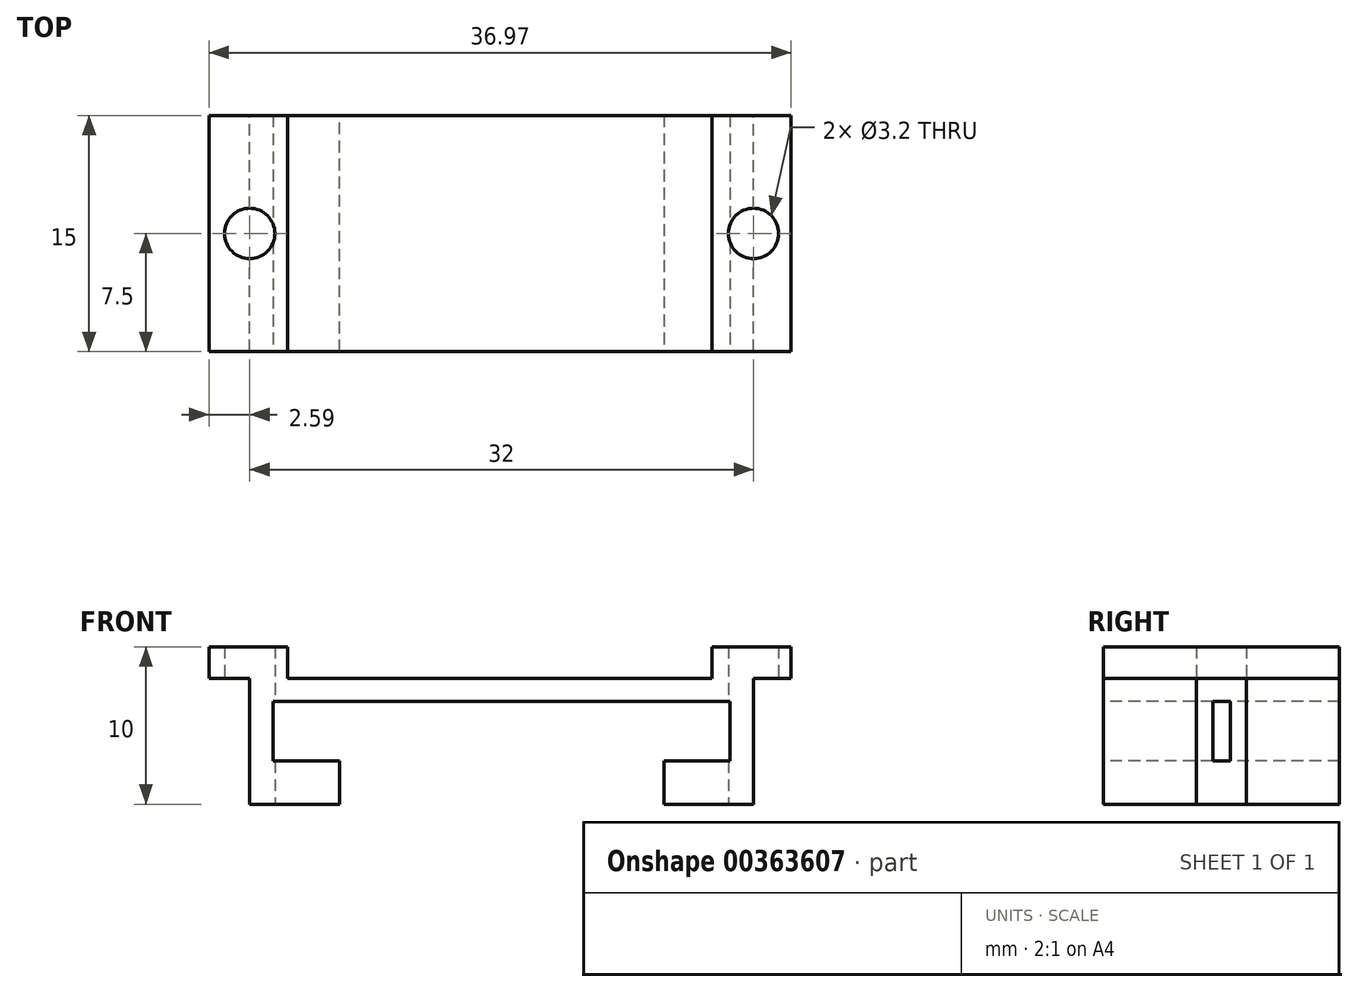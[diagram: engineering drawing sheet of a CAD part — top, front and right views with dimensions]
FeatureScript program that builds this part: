
annotation { "Feature Type Name" : "Feature", "Feature Type Description" : "" }
export const myFeature = defineFeature(function(context is Context, id is Id, definition is map)
    precondition{}
    {
        {
            var Q0;
            Q0=qCreatedBy(makeId("Top.planeOp"),FACE);
            var sketch = newSketch(context, id + "F0", { "sketchPlane" : qUnion([Q0])});
            skLineSegment(sketch, "E0.bottom", {"start": v(16, -7.5) * mm, "end": v(-16, -7.5) * mm});
            skLineSegment(sketch, "E0.top", {"start": v(16, 7.5) * mm, "end": v(-16, 7.5) * mm});
            skLineSegment(sketch, "E0.left", {"start": v(16, -7.5) * mm, "end": v(16, 7.5) * mm});
            skLineSegment(sketch, "E0.right", {"start": v(-16, -7.5) * mm, "end": v(-16, 7.5) * mm});
            skPoint(sketch, "E0.middle", {"position": v(0, 0) * mm});
            skSolve(sketch);
        }
        {
            var Q0;
            Q0=makeQuery(id+"F0.imprint","IMPRINT",FACE,{"disambiguationData":[TD([[makeQuery(id+"F0.imprint","IMPRINT",EDGE,{"derivedFrom":sQuery(id+"F0.wireOp",EDGE,"E0.bottom")}),-1.0]])]});
            extrude(context, id + "F1", {"entities" : qUnion([Q0]), "depth" : 8 * mm});
        }
        {
            var Q0;
            Q0=makeQuery(id+"F1.opExtrude","SWEPT_FACE",FACE,{"disambiguationData":[OSD([sQuery(id+"F0.wireOp",EDGE,"E0.bottom")])]});
            var sketch = newSketch(context, id + "F2", { "sketchPlane" : qUnion([Q0])});
            skLineSegment(sketch, "E1.bottom", {"start": v(14.5, 2.74) * mm, "end": v(-14.5, 2.74) * mm});
            skLineSegment(sketch, "E1.top", {"start": v(14.5, 6.54) * mm, "end": v(-14.5, 6.54) * mm});
            skLineSegment(sketch, "E1.left", {"start": v(14.5, 2.74) * mm, "end": v(14.5, 6.54) * mm});
            skLineSegment(sketch, "E1.right", {"start": v(-14.5, 2.74) * mm, "end": v(-14.5, 6.54) * mm});
            skPoint(sketch, "E1.middle", {"position": v(0, 4.64) * mm});
            skSolve(sketch);
        }
        {
            var Q0;
            Q0=makeQuery(id+"F2.imprint","IMPRINT",FACE,{"disambiguationData":[TD([[makeQuery(id+"F2.imprint","IMPRINT",EDGE,{"derivedFrom":sQuery(id+"F2.wireOp",EDGE,"E1.bottom")}),-1.0]])]});
            extrude(context, id + "F3", {"entities" : qUnion([Q0]), "operationType" : NewBodyOperationType.REMOVE, "oppositeDirection" : true, "depth" : 30 * mm});
        }
        {
            var Q0;
            Q0=makeQuery(id+"F1.opExtrude","CAP_FACE",FACE,{"disambiguationData":[OSD([sQuery(id+"F0.wireOp",EDGE,"E0.bottom"),sQuery(id+"F0.wireOp",EDGE,"E0.top"),sQuery(id+"F0.wireOp",EDGE,"E0.left"),sQuery(id+"F0.wireOp",EDGE,"E0.right")])],"isStart":false});
            var sketch = newSketch(context, id + "F4", { "sketchPlane" : qUnion([Q0])});
            skLineSegment(sketch, "E2.bottom", {"start": v(-13.6, 7.5) * mm, "end": v(-18.6, 7.5) * mm});
            skLineSegment(sketch, "E2.top", {"start": v(-13.6, -7.5) * mm, "end": v(-18.6, -7.5) * mm});
            skLineSegment(sketch, "E2.left", {"start": v(-13.6, 7.5) * mm, "end": v(-13.6, -7.5) * mm});
            skLineSegment(sketch, "E2.right", {"start": v(-18.6, 7.5) * mm, "end": v(-18.6, -7.5) * mm});
            skLineSegment(sketch, "E3.bottom", {"start": v(13.38, 7.5) * mm, "end": v(18.38, 7.5) * mm});
            skLineSegment(sketch, "E3.top", {"start": v(13.38, -7.5) * mm, "end": v(18.38, -7.5) * mm});
            skLineSegment(sketch, "E3.left", {"start": v(13.38, 7.5) * mm, "end": v(13.38, -7.5) * mm});
            skLineSegment(sketch, "E3.right", {"start": v(18.38, 7.5) * mm, "end": v(18.38, -7.5) * mm});
            skPoint(sketch, "E4", {"position": v(-16, 0) * mm});
            skPoint(sketch, "E5", {"position": v(16, 0) * mm});
            skPoint(sketch, "E5.positionSnap0", {"position": v(16, 0) * mm});
            skCircle(sketch, "E6", {"center": v(-16, 0) * mm, "radius": 1.6 * mm});
            skCircle(sketch, "E7", {"center": v(16, 0) * mm, "radius": 1.6 * mm});
            skSolve(sketch);
        }
        {
            var Q0;
            {var subQ2=sQuery(id+"F4.wireOp",EDGE,"E3.right");Q0=makeQuery(id+"F4.imprint","IMPRINT",FACE,{"disambiguationData":[TD([[makeQuery(id+"F4.imprint","IMPRINT",EDGE,{"derivedFrom":subQ2}),-1.0]])]});}
            var Q1;
            {var subQ2=sQuery(id+"F4.wireOp",EDGE,"E3.left");Q1=makeQuery(id+"F4.imprint","IMPRINT",FACE,{"disambiguationData":[TD([[makeQuery(id+"F4.imprint","IMPRINT",EDGE,{"derivedFrom":subQ2}),1.0]])]});}
            var Q2;
            {var subQ2=sQuery(id+"F4.wireOp",EDGE,"E2.right");Q2=makeQuery(id+"F4.imprint","IMPRINT",FACE,{"disambiguationData":[TD([[makeQuery(id+"F4.imprint","IMPRINT",EDGE,{"derivedFrom":subQ2}),1.0]])]});}
            var Q3;
            {var subQ2=sQuery(id+"F4.wireOp",EDGE,"E2.left");Q3=makeQuery(id+"F4.imprint","IMPRINT",FACE,{"disambiguationData":[TD([[makeQuery(id+"F4.imprint","IMPRINT",EDGE,{"derivedFrom":subQ2}),-1.0]])]});}
            extrude(context, id + "F5", {"entities" : qUnion([Q0, Q1, Q2, Q3]), "operationType" : NewBodyOperationType.ADD, "depth" : 2 * mm});
        }
        {
            var Q0;
            Q0=makeQuery(id+"F1.opExtrude","CAP_FACE",FACE,{"disambiguationData":[OSD([sQuery(id+"F0.wireOp",EDGE,"E0.bottom"),sQuery(id+"F0.wireOp",EDGE,"E0.top"),sQuery(id+"F0.wireOp",EDGE,"E0.left"),sQuery(id+"F0.wireOp",EDGE,"E0.right")])],"isStart":true});
            var sketch = newSketch(context, id + "F6", { "sketchPlane" : qUnion([Q0])});
            skLineSegment(sketch, "E8.bottom", {"start": v(10.3, -9.2) * mm, "end": v(-10.3, -9.2) * mm});
            skLineSegment(sketch, "E8.top", {"start": v(10.3, 9.2) * mm, "end": v(-10.3, 9.2) * mm});
            skLineSegment(sketch, "E8.left", {"start": v(10.3, -9.2) * mm, "end": v(10.3, 9.2) * mm});
            skLineSegment(sketch, "E8.right", {"start": v(-10.3, -9.2) * mm, "end": v(-10.3, 9.2) * mm});
            skPoint(sketch, "E8.middle", {"position": v(0, 0) * mm});
            skSolve(sketch);
        }
        {
            var Q0;
            {var subQ0=sQuery(id+"F6.wireOp",EDGE,"E8.left");var subQ1=makeQuery(id+"F1.opExtrude","CAP_EDGE",EDGE,{"disambiguationData":[OSD([sQuery(id+"F0.wireOp",EDGE,"E0.top")])],"isStart":true});var subQ2=makeQuery(id+"F6.imprint","INTERSECT",VERTEX,{"derivedFrom":[subQ1,subQ0]});Q0=makeQuery(id+"F6.imprint","IMPRINT",FACE,{"disambiguationData":[TD([[makeQuery(id+"F6.imprint","IMPRINT",EDGE,{"disambiguationData":[TD([[subQ2,-1.0]])],"derivedFrom":subQ0}),1.0]])]});}
            extrude(context, id + "F7", {"entities" : qUnion([Q0]), "operationType" : NewBodyOperationType.REMOVE, "oppositeDirection" : true, "depth" : 5 * mm});
        }
        {
            var Q0;
            {var subQ0=sQuery(id+"F4.wireOp",EDGE,"E6");var subQ1=makeQuery(id+"F1.opExtrude","CAP_EDGE",EDGE,{"disambiguationData":[OSD([sQuery(id+"F0.wireOp",EDGE,"E0.right")])],"isStart":false});var subQ2=makeQuery(id+"F4.imprint","INTERSECT",VERTEX,{"disambiguationData":[OD(0.0)],"derivedFrom":[subQ1,subQ0]});Q0=makeQuery(id+"F4.imprint","IMPRINT",FACE,{"disambiguationData":[TD([[makeQuery(id+"F4.imprint","IMPRINT",EDGE,{"disambiguationData":[TD([[subQ2,-1.0]])],"derivedFrom":subQ0}),1.0]])]});}
            var Q1;
            {var subQ0=sQuery(id+"F4.wireOp",EDGE,"E6");var subQ1=makeQuery(id+"F1.opExtrude","CAP_EDGE",EDGE,{"disambiguationData":[OSD([sQuery(id+"F0.wireOp",EDGE,"E0.right")])],"isStart":false});var subQ2=makeQuery(id+"F4.imprint","INTERSECT",VERTEX,{"disambiguationData":[OD(0.0)],"derivedFrom":[subQ1,subQ0]});Q1=makeQuery(id+"F4.imprint","IMPRINT",FACE,{"disambiguationData":[TD([[makeQuery(id+"F4.imprint","IMPRINT",EDGE,{"disambiguationData":[TD([[subQ2,1.0]])],"derivedFrom":subQ0}),1.0]])]});}
            var Q2;
            {var subQ0=sQuery(id+"F4.wireOp",EDGE,"E7");var subQ1=makeQuery(id+"F1.opExtrude","CAP_EDGE",EDGE,{"disambiguationData":[OSD([sQuery(id+"F0.wireOp",EDGE,"E0.left")])],"isStart":false});var subQ2=makeQuery(id+"F4.imprint","INTERSECT",VERTEX,{"disambiguationData":[OD(0.0)],"derivedFrom":[subQ1,subQ0]});Q2=makeQuery(id+"F4.imprint","IMPRINT",FACE,{"disambiguationData":[TD([[makeQuery(id+"F4.imprint","IMPRINT",EDGE,{"disambiguationData":[TD([[subQ2,1.0]])],"derivedFrom":subQ0}),1.0]])]});}
            var Q3;
            {var subQ0=sQuery(id+"F4.wireOp",EDGE,"E7");var subQ1=makeQuery(id+"F1.opExtrude","CAP_EDGE",EDGE,{"disambiguationData":[OSD([sQuery(id+"F0.wireOp",EDGE,"E0.left")])],"isStart":false});var subQ2=makeQuery(id+"F4.imprint","INTERSECT",VERTEX,{"disambiguationData":[OD(0.0)],"derivedFrom":[subQ1,subQ0]});Q3=makeQuery(id+"F4.imprint","IMPRINT",FACE,{"disambiguationData":[TD([[makeQuery(id+"F4.imprint","IMPRINT",EDGE,{"disambiguationData":[TD([[subQ2,-1.0]])],"derivedFrom":subQ0}),1.0]])]});}
            extrude(context, id + "F8", {"entities" : qUnion([Q0, Q1, Q2, Q3]), "operationType" : NewBodyOperationType.REMOVE, "oppositeDirection" : true, "depth" : 25 * mm});
        }
    });
